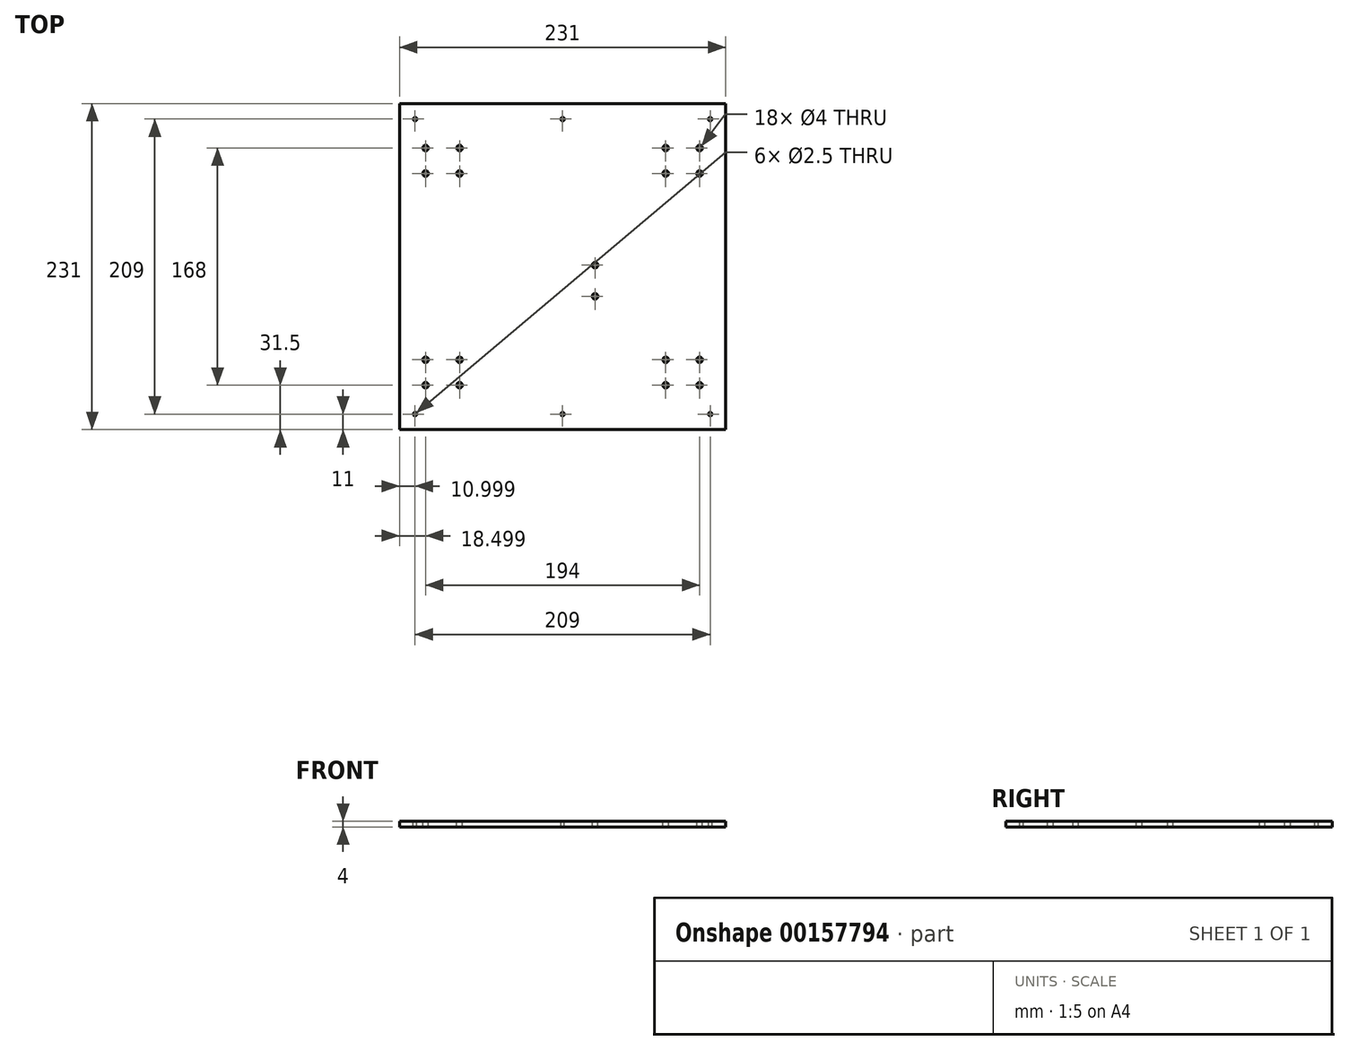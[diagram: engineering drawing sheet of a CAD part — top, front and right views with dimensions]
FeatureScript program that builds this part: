
annotation { "Feature Type Name" : "Feature", "Feature Type Description" : "" }
export const myFeature = defineFeature(function(context is Context, id is Id, definition is map)
    precondition{}
    {
        {
            var Q0;
            Q0=qCreatedBy(makeId("Top.planeOp"),FACE);
            var sketch = newSketch(context, id + "F0", { "sketchPlane" : qUnion([Q0])});
            skLineSegment(sketch, "E0.bottom", {"start": v(-115.9, 135.57) * mm, "end": v(115.1, 135.57) * mm});
            skLineSegment(sketch, "E0.top", {"start": v(-115.9, -95.43) * mm, "end": v(115.1, -95.43) * mm});
            skLineSegment(sketch, "E0.left", {"start": v(-115.9, 135.57) * mm, "end": v(-115.9, -95.43) * mm});
            skLineSegment(sketch, "E0.right", {"start": v(115.1, 135.57) * mm, "end": v(115.1, -95.43) * mm});
            skSolve(sketch);
        }
        {
            var Q0;
            Q0 = qSketchRegion(id + "F0", true);
            extrude(context, id + "F1", {"entities" : qUnion([Q0]), "oppositeDirection" : true, "depth" : 4 * mm});
        }
        {
            var Q0;
            Q0=makeQuery(id+"F1.opExtrude","CAP_FACE",FACE,{"disambiguationData":[OSD([sQuery(id+"F0.wireOp",EDGE,"E0.bottom"),sQuery(id+"F0.wireOp",EDGE,"E0.top"),sQuery(id+"F0.wireOp",EDGE,"E0.left"),sQuery(id+"F0.wireOp",EDGE,"E0.right")])],"isStart":true});
            var sketch = newSketch(context, id + "F2", { "sketchPlane" : qUnion([Q0])});
            skCircle(sketch, "E1", {"center": v(72.6, 104.07) * mm, "radius": 2 * mm});
            skCircle(sketch, "E2", {"center": v(96.6, 104.07) * mm, "radius": 2 * mm});
            skCircle(sketch, "E3", {"center": v(72.6, 86.07) * mm, "radius": 2 * mm});
            skCircle(sketch, "E4", {"center": v(96.6, 86.07) * mm, "radius": 2 * mm});
            skCircle(sketch, "E5", {"center": v(-97.4, 104.07) * mm, "radius": 2 * mm});
            skCircle(sketch, "E6", {"center": v(-73.4, 104.07) * mm, "radius": 2 * mm});
            skCircle(sketch, "E7", {"center": v(-97.4, 86.07) * mm, "radius": 2 * mm});
            skCircle(sketch, "E8", {"center": v(-73.4, 86.07) * mm, "radius": 2 * mm});
            skCircle(sketch, "E9", {"center": v(72.6, -45.93) * mm, "radius": 2 * mm});
            skCircle(sketch, "E10", {"center": v(96.6, -45.93) * mm, "radius": 2 * mm});
            skCircle(sketch, "E11", {"center": v(72.6, -63.93) * mm, "radius": 2 * mm});
            skCircle(sketch, "E12", {"center": v(96.6, -63.93) * mm, "radius": 2 * mm});
            skCircle(sketch, "E13", {"center": v(-97.4, -45.93) * mm, "radius": 2 * mm});
            skCircle(sketch, "E14", {"center": v(-73.4, -45.93) * mm, "radius": 2 * mm});
            skCircle(sketch, "E15", {"center": v(-97.4, -63.93) * mm, "radius": 2 * mm});
            skCircle(sketch, "E16", {"center": v(-73.4, -63.93) * mm, "radius": 2 * mm});
            skLineSegment(sketch, "E17", {"start": v(-0.4, -95.43) * mm, "end": v(-0.4, 135.57) * mm, "construction": true});
            skLineSegment(sketch, "E18", {"start": v(-115.9, 20.07) * mm, "end": v(115.1, 20.07) * mm, "construction": true});
            skLineSegment(sketch, "E19", {"start": v(-73.4, -45.93) * mm, "end": v(-0.4, -45.93) * mm, "construction": true});
            skLineSegment(sketch, "E20", {"start": v(-0.4, -45.93) * mm, "end": v(72.6, -45.93) * mm, "construction": true});
            skLineSegment(sketch, "E21", {"start": v(-73.4, -45.93) * mm, "end": v(-73.4, 20.07) * mm, "construction": true});
            skLineSegment(sketch, "E22", {"start": v(-73.4, 20.07) * mm, "end": v(-73.4, 86.07) * mm, "construction": true});
            skCircle(sketch, "E23", {"center": v(-104.9, -84.43) * mm, "radius": 1.25 * mm});
            skCircle(sketch, "E24", {"center": v(-104.9, 124.57) * mm, "radius": 1.25 * mm});
            skCircle(sketch, "E25", {"center": v(104.1, 124.57) * mm, "radius": 1.25 * mm});
            skCircle(sketch, "E26", {"center": v(104.1, -84.43) * mm, "radius": 1.25 * mm});
            skLineSegment(sketch, "E27", {"start": v(104.1, 124.57) * mm, "end": v(-0.4, 124.57) * mm, "construction": true});
            skLineSegment(sketch, "E28", {"start": v(-0.4, 124.57) * mm, "end": v(-104.9, 124.57) * mm, "construction": true});
            skLineSegment(sketch, "E29", {"start": v(104.1, -84.43) * mm, "end": v(104.1, 20.07) * mm, "construction": true});
            skLineSegment(sketch, "E30", {"start": v(104.1, 20.07) * mm, "end": v(104.1, 124.57) * mm, "construction": true});
            skCircle(sketch, "E31", {"center": v(-0.4, 124.57) * mm, "radius": 1.25 * mm});
            skLineSegment(sketch, "E32", {"start": v(-104.9, -84.43) * mm, "end": v(-0.4, -84.43) * mm, "construction": true});
            skCircle(sketch, "E33", {"center": v(-0.4, -84.43) * mm, "radius": 1.25 * mm});
            skCircle(sketch, "E34", {"center": v(22.6, -0.93) * mm, "radius": 2 * mm});
            skCircle(sketch, "E35", {"center": v(22.6, 21.07) * mm, "radius": 2 * mm});
            skSolve(sketch);
        }
        {
            var Q0;
            Q0=makeQuery(id+"F2.imprint","IMPRINT",FACE,{"disambiguationData":[TD([[makeQuery(id+"F2.imprint","IMPRINT",EDGE,{"derivedFrom":sQuery(id+"F2.wireOp",EDGE,"E1")}),-1.0]])]});
            extrude(context, id + "F3", {"entities" : qUnion([Q0]), "operationType" : NewBodyOperationType.INTERSECT, "oppositeDirection" : true, "depth" : 4 * mm});
        }
    });
